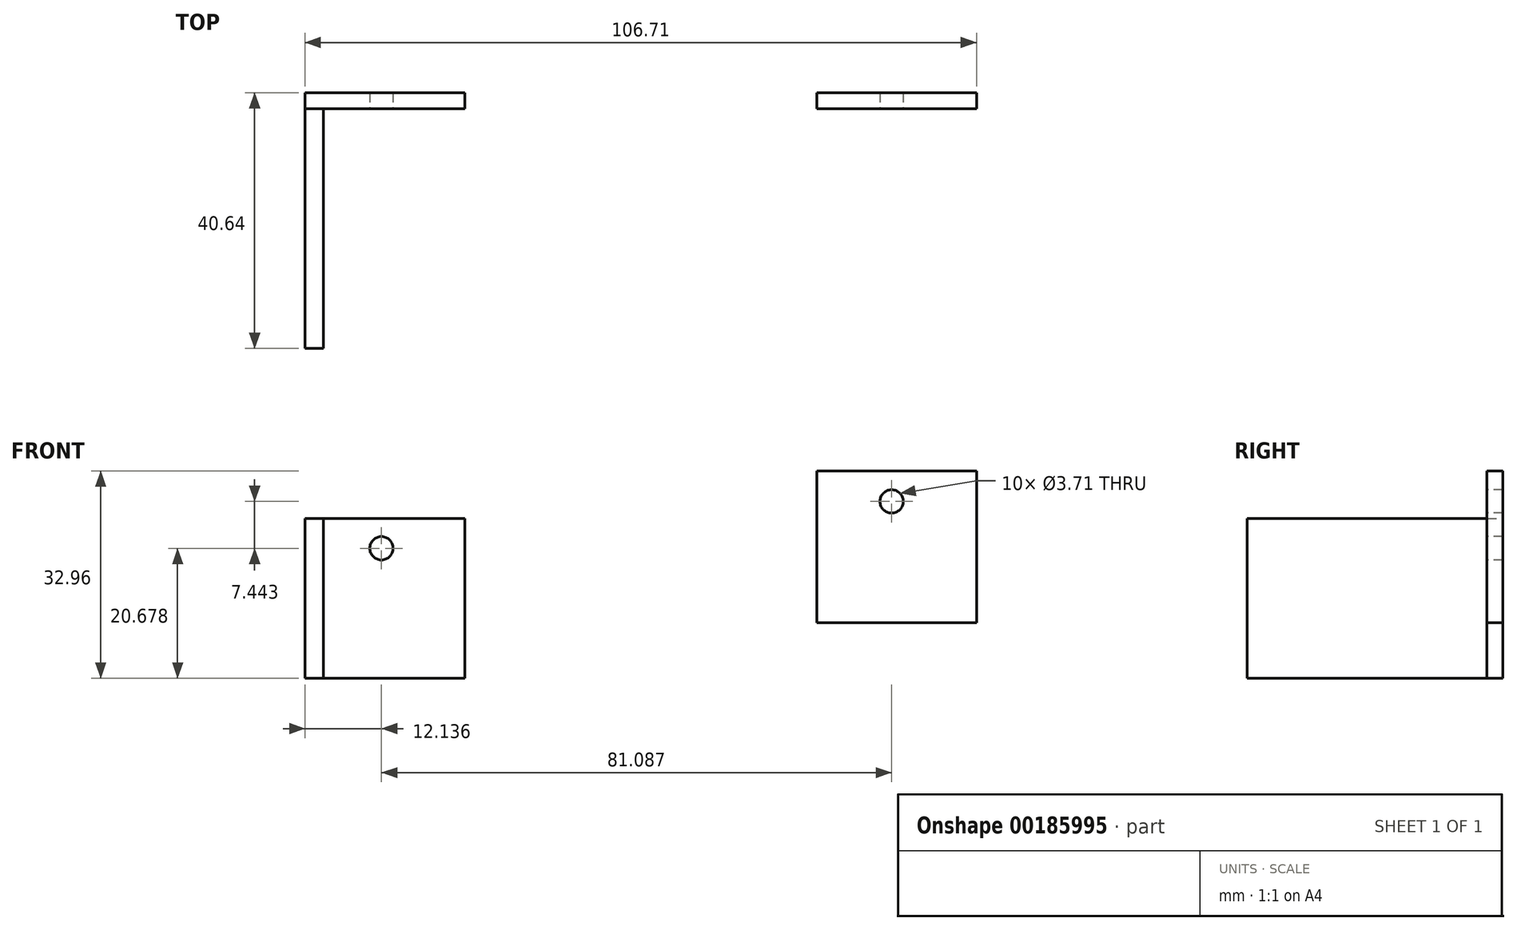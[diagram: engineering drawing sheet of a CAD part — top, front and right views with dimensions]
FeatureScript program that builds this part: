
annotation { "Feature Type Name" : "Feature", "Feature Type Description" : "" }
export const myFeature = defineFeature(function(context is Context, id is Id, definition is map)
    precondition{}
    {
        {
            var Q0;
            Q0=qCreatedBy(makeId("Front.planeOp"),FACE);
            var sketch = newSketch(context, id + "F0", { "sketchPlane" : qUnion([Q0])});
            skLineSegment(sketch, "E0.bottom", {"start": v(-68.74, -44.28) * mm, "end": v(-43.34, -44.28) * mm});
            skLineSegment(sketch, "E0.top", {"start": v(-68.74, -18.88) * mm, "end": v(-43.34, -18.88) * mm});
            skLineSegment(sketch, "E0.left", {"start": v(-68.74, -44.28) * mm, "end": v(-68.74, -18.88) * mm});
            skLineSegment(sketch, "E0.right", {"start": v(-43.34, -44.28) * mm, "end": v(-43.34, -18.88) * mm});
            skLineSegment(sketch, "E1.bottom", {"start": v(12.57, -35.44) * mm, "end": v(37.97, -35.44) * mm});
            skLineSegment(sketch, "E1.top", {"start": v(12.57, -11.32) * mm, "end": v(37.97, -11.32) * mm});
            skLineSegment(sketch, "E1.left", {"start": v(12.57, -35.44) * mm, "end": v(12.57, -11.32) * mm});
            skLineSegment(sketch, "E1.right", {"start": v(37.97, -35.44) * mm, "end": v(37.97, -11.32) * mm});
            skSolve(sketch);
        }
        {
            var Q0;
            Q0=makeQuery(id+"F0.imprint","IMPRINT",FACE,{"disambiguationData":[TD([[makeQuery(id+"F0.imprint","IMPRINT",EDGE,{"derivedFrom":sQuery(id+"F0.wireOp",EDGE,"E1.bottom")}),1.0]])]});
            var Q1;
            Q1=makeQuery(id+"F0.imprint","IMPRINT",FACE,{"disambiguationData":[TD([[makeQuery(id+"F0.imprint","IMPRINT",EDGE,{"derivedFrom":sQuery(id+"F0.wireOp",EDGE,"E0.bottom")}),1.0]])]});
            extrude(context, id + "F1", {"entities" : qUnion([Q0, Q1]), "depth" : 2.54 * mm});
        }
        {
            var Q0;
            Q0=makeQuery(id+"F1.opExtrude","CAP_FACE",FACE,{"disambiguationData":[OSD([sQuery(id+"F0.wireOp",EDGE,"E0.bottom"),sQuery(id+"F0.wireOp",EDGE,"E0.top"),sQuery(id+"F0.wireOp",EDGE,"E0.left"),sQuery(id+"F0.wireOp",EDGE,"E0.right")])],"isStart":false});
            var sketch = newSketch(context, id + "F2", { "sketchPlane" : qUnion([Q0])});
            skLineSegment(sketch, "E2.bottom", {"start": v(-68.74, -18.88) * mm, "end": v(-65.8, -18.88) * mm});
            skLineSegment(sketch, "E2.top", {"start": v(-68.74, -44.28) * mm, "end": v(-65.8, -44.28) * mm});
            skLineSegment(sketch, "E2.left", {"start": v(-68.74, -18.88) * mm, "end": v(-68.74, -44.28) * mm});
            skLineSegment(sketch, "E2.right", {"start": v(-65.8, -18.88) * mm, "end": v(-65.8, -44.28) * mm});
            skSolve(sketch);
        }
        {
            var Q0;
            Q0=makeQuery(id+"F1.opExtrude","CAP_FACE",FACE,{"disambiguationData":[OSD([sQuery(id+"F0.wireOp",EDGE,"E1.bottom"),sQuery(id+"F0.wireOp",EDGE,"E1.top"),sQuery(id+"F0.wireOp",EDGE,"E1.left"),sQuery(id+"F0.wireOp",EDGE,"E1.right")])],"isStart":false});
            var sketch = newSketch(context, id + "F3", { "sketchPlane" : qUnion([Q0])});
            skLineSegment(sketch, "E3.bottom", {"start": v(37.97, -11.32) * mm, "end": v(35.04, -11.32) * mm});
            skLineSegment(sketch, "E3.top", {"start": v(37.97, -35.44) * mm, "end": v(35.04, -35.44) * mm});
            skLineSegment(sketch, "E3.left", {"start": v(37.97, -11.32) * mm, "end": v(37.97, -35.44) * mm});
            skLineSegment(sketch, "E3.right", {"start": v(35.04, -11.32) * mm, "end": v(35.04, -35.44) * mm});
            skSolve(sketch);
        }
        {
            var Q0;
            Q0=makeQuery(id+"F2.imprint","IMPRINT",FACE,{"disambiguationData":[TD([[makeQuery(id+"F2.imprint","IMPRINT",EDGE,{"derivedFrom":sQuery(id+"F2.wireOp",EDGE,"E2.bottom")}),-1.0]])]});
            var Q1;
            Q1=makeQuery(id+"F3.imprint","IMPRINT",FACE,{"disambiguationData":[TD([[makeQuery(id+"F3.imprint","IMPRINT",EDGE,{"derivedFrom":sQuery(id+"F3.wireOp",EDGE,"E3.bottom")}),-1.0]])]});
            extrude(context, id + "F4", {"entities" : qUnion([Q0, Q1]), "depth" : 38.1 * mm});
        }
        {
            var Q0;
            Q0=makeQuery(id+"F1.opExtrude","CAP_FACE",FACE,{"disambiguationData":[OSD([sQuery(id+"F0.wireOp",EDGE,"E0.bottom"),sQuery(id+"F0.wireOp",EDGE,"E0.top"),sQuery(id+"F0.wireOp",EDGE,"E0.left"),sQuery(id+"F0.wireOp",EDGE,"E0.right")])],"isStart":false});
            var sketch = newSketch(context, id + "F5", { "sketchPlane" : qUnion([Q0])});
            skCircle(sketch, "E4", {"center": v(-56.6, -23.6) * mm, "radius": 1.85 * mm});
            skSolve(sketch);
        }
        {
            var Q0;
            Q0=sQuery(id+"F5.wireOp",VERTEX,"E4.center");
            var Q1;
            Q1=makeQuery(id+"F1.opExtrude","SWEPT_BODY",BODY,{"disambiguationData":[OSD([sQuery(id+"F0.wireOp",EDGE,"E0.bottom"),sQuery(id+"F0.wireOp",EDGE,"E0.top"),sQuery(id+"F0.wireOp",EDGE,"E0.left"),sQuery(id+"F0.wireOp",EDGE,"E0.right")])]});
            hole(context, id + "F6", {"style" : HoleStyle.SIMPLE, "endStyle" : HoleEndStyle.BLIND, "holeDiameter" : 3.7 * mm, "holeDepth" : 12.7 * mm, "locations" : qUnion([Q0]), "scope" : qUnion([Q1])});
        }
        {
            var Q0;
            Q0=makeQuery(id+"F1.opExtrude","CAP_FACE",FACE,{"disambiguationData":[OSD([sQuery(id+"F0.wireOp",EDGE,"E1.bottom"),sQuery(id+"F0.wireOp",EDGE,"E1.top"),sQuery(id+"F0.wireOp",EDGE,"E1.left"),sQuery(id+"F0.wireOp",EDGE,"E1.right")])],"isStart":false});
            var sketch = newSketch(context, id + "F7", { "sketchPlane" : qUnion([Q0])});
            skCircle(sketch, "E5", {"center": v(24.48, -16.16) * mm, "radius": 1.85 * mm});
            skSolve(sketch);
        }
        {
            var Q0;
            Q0=sQuery(id+"F7.wireOp",VERTEX,"E5.center");
            var Q1;
            Q1=makeQuery(id+"F1.opExtrude","SWEPT_BODY",BODY,{"disambiguationData":[OSD([sQuery(id+"F0.wireOp",EDGE,"E1.bottom"),sQuery(id+"F0.wireOp",EDGE,"E1.top"),sQuery(id+"F0.wireOp",EDGE,"E1.left"),sQuery(id+"F0.wireOp",EDGE,"E1.right")])]});
            hole(context, id + "F8", {"style" : HoleStyle.SIMPLE, "endStyle" : HoleEndStyle.BLIND, "holeDiameter" : 3.7 * mm, "holeDepth" : 12.7 * mm, "locations" : qUnion([Q0]), "scope" : qUnion([Q1])});
        }
        {
            var Q0;
            Q0=makeQuery(id+"F4.opExtrude","SWEPT_BODY",BODY,{"disambiguationData":[OSD([sQuery(id+"F3.wireOp",EDGE,"E3.bottom"),sQuery(id+"F3.wireOp",EDGE,"E3.top"),sQuery(id+"F3.wireOp",EDGE,"E3.left"),sQuery(id+"F3.wireOp",EDGE,"E3.right")])]});
            deleteBodies(context, id + "F9", {"entities" : qUnion([Q0])});
        }
        {
            var Q0;
            Q0=makeQuery(id+"F1.opExtrude","CAP_FACE",FACE,{"disambiguationData":[OSD([sQuery(id+"F0.wireOp",EDGE,"E0.bottom"),sQuery(id+"F0.wireOp",EDGE,"E0.top"),sQuery(id+"F0.wireOp",EDGE,"E0.left"),sQuery(id+"F0.wireOp",EDGE,"E0.right")])],"isStart":false});
            var sketch = newSketch(context, id + "F10", { "sketchPlane" : qUnion([Q0])});
            skCircle(sketch, "E6", {"center": v(-56.07, -41.62) * mm, "radius": 1.85 * mm});
            skSolve(sketch);
        }
        {
            var Q0;
            Q0=sQuery(id+"F10.wireOp",VERTEX,"E6.center");
            var Q1;
            Q1=makeQuery(id+"F4.opExtrude","SWEPT_BODY",BODY,{"disambiguationData":[OSD([sQuery(id+"F2.wireOp",EDGE,"E2.bottom"),sQuery(id+"F2.wireOp",EDGE,"E2.top"),sQuery(id+"F2.wireOp",EDGE,"E2.left"),sQuery(id+"F2.wireOp",EDGE,"E2.right")])]});
            hole(context, id + "F11", {"style" : HoleStyle.SIMPLE, "endStyle" : HoleEndStyle.BLIND, "holeDiameter" : 3.7 * mm, "holeDepth" : 12.7 * mm, "locations" : qUnion([Q0]), "scope" : qUnion([Q1])});
        }
    });
